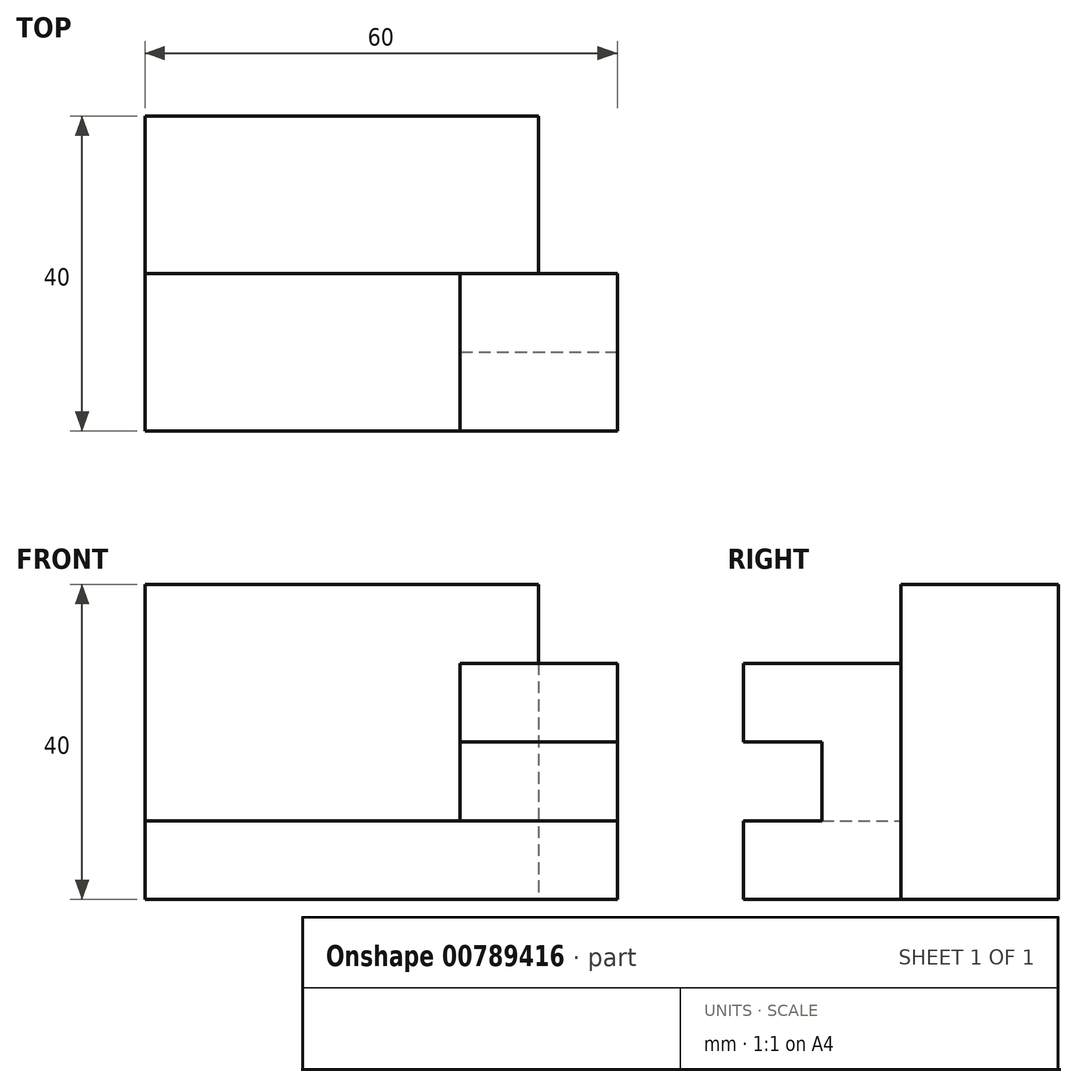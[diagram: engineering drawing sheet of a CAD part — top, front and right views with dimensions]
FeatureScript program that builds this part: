
annotation { "Feature Type Name" : "Feature", "Feature Type Description" : "" }
export const myFeature = defineFeature(function(context is Context, id is Id, definition is map)
    precondition{}
    {
        {
            var Q0;
            Q0=qCreatedBy(makeId("Top.planeOp"),FACE);
            var sketch = newSketch(context, id + "F0", { "sketchPlane" : qUnion([Q0])});
            skLineSegment(sketch, "E0", {"start": v(0, 0) * mm, "end": v(0, 40) * mm});
            skLineSegment(sketch, "E1", {"start": v(0, 40) * mm, "end": v(50, 40) * mm});
            skLineSegment(sketch, "E2", {"start": v(60, 0) * mm, "end": v(0, 0) * mm});
            skLineSegment(sketch, "E3", {"start": v(0, 20) * mm, "end": v(50, 20) * mm});
            skLineSegment(sketch, "E4", {"start": v(50, 20) * mm, "end": v(50, 40) * mm});
            skLineSegment(sketch, "E5", {"start": v(50, 20) * mm, "end": v(60, 20) * mm});
            skLineSegment(sketch, "E6", {"start": v(60, 20) * mm, "end": v(60, 0) * mm});
            skSolve(sketch);
        }
        {
            var Q0;
            {var subQ0=sQuery(id+"F0.wireOp",EDGE,"E1");Q0=makeQuery(id+"F0.imprint","IMPRINT",FACE,{"disambiguationData":[TD([[makeQuery(id+"F0.imprint","IMPRINT",EDGE,{"derivedFrom":subQ0}),-1.0]])]});}
            extrude(context, id + "F1", {"entities" : qUnion([Q0]), "depth" : 40 * mm, "offsetDistance" : 25 * mm});
        }
        {
            var Q0;
            Q0=qCreatedBy(makeId("Top.planeOp"),FACE);
            var sketch = newSketch(context, id + "F2", { "sketchPlane" : qUnion([Q0])});
            skLineSegment(sketch, "E7", {"start": v(0, 0) * mm, "end": v(0, 20) * mm});
            skLineSegment(sketch, "E8", {"start": v(60, 0) * mm, "end": v(0, 0) * mm});
            skLineSegment(sketch, "E9", {"start": v(60, 0) * mm, "end": v(60, 20) * mm});
            skLineSegment(sketch, "E10", {"start": v(60, 20) * mm, "end": v(0, 20) * mm});
            skSolve(sketch);
        }
        {
            var Q0;
            Q0 = qSketchRegion(id + "F2", true);
            extrude(context, id + "F3", {"entities" : qUnion([Q0]), "operationType" : NewBodyOperationType.ADD, "depth" : 10 * mm, "offsetDistance" : 25 * mm});
        }
        {
            var Q0;
            Q0=makeQuery(id+"F3.opExtrude","CAP_FACE",FACE,{"disambiguationData":[OSD([sQuery(id+"F2.wireOp",EDGE,"E7"),sQuery(id+"F2.wireOp",EDGE,"E8"),sQuery(id+"F2.wireOp",EDGE,"E9"),sQuery(id+"F2.wireOp",EDGE,"E10")])],"isStart":false});
            var sketch = newSketch(context, id + "F4", { "sketchPlane" : qUnion([Q0])});
            skLineSegment(sketch, "E11", {"start": v(60, 0) * mm, "end": v(60, 20) * mm});
            skLineSegment(sketch, "E12", {"start": v(60, 20) * mm, "end": v(60, 0) * mm});
            skLineSegment(sketch, "E13", {"start": v(60, 0) * mm, "end": v(40, 0) * mm});
            skLineSegment(sketch, "E14", {"start": v(40, 20) * mm, "end": v(60, 20) * mm});
            skLineSegment(sketch, "E15", {"start": v(40, 0) * mm, "end": v(40, 20) * mm});
            skSolve(sketch);
        }
        {
            var Q0;
            Q0 = qSketchRegion(id + "F4", true);
            extrude(context, id + "F5", {"entities" : qUnion([Q0]), "operationType" : NewBodyOperationType.ADD, "depth" : 20 * mm, "offsetDistance" : 25 * mm});
        }
        {
            var Q0;
            Q0=makeQuery(id+"F5.opExtrude","SWEPT_FACE",FACE,{"disambiguationData":[OSD([sQuery(id+"F4.wireOp",EDGE,"E15")])]});
            var sketch = newSketch(context, id + "F6", { "sketchPlane" : qUnion([Q0])});
            skLineSegment(sketch, "E16", {"start": v(0, 10) * mm, "end": v(0, 20) * mm});
            skLineSegment(sketch, "E17", {"start": v(0, 20) * mm, "end": v(-10, 20) * mm});
            skPoint(sketch, "E17.endSnap0", {"position": v(-10, 10) * mm});
            skLineSegment(sketch, "E18", {"start": v(-10, 20) * mm, "end": v(-10, 10) * mm});
            skLineSegment(sketch, "E19", {"start": v(0, 10) * mm, "end": v(-10, 10) * mm});
            skSolve(sketch);
        }
        {
            var Q0;
            Q0 = qSketchRegion(id + "F6", true);
            extrude(context, id + "F7", {"entities" : qUnion([Q0]), "operationType" : NewBodyOperationType.REMOVE, "oppositeDirection" : true, "depth" : 25 * mm, "offsetDistance" : 25 * mm});
        }
    });
